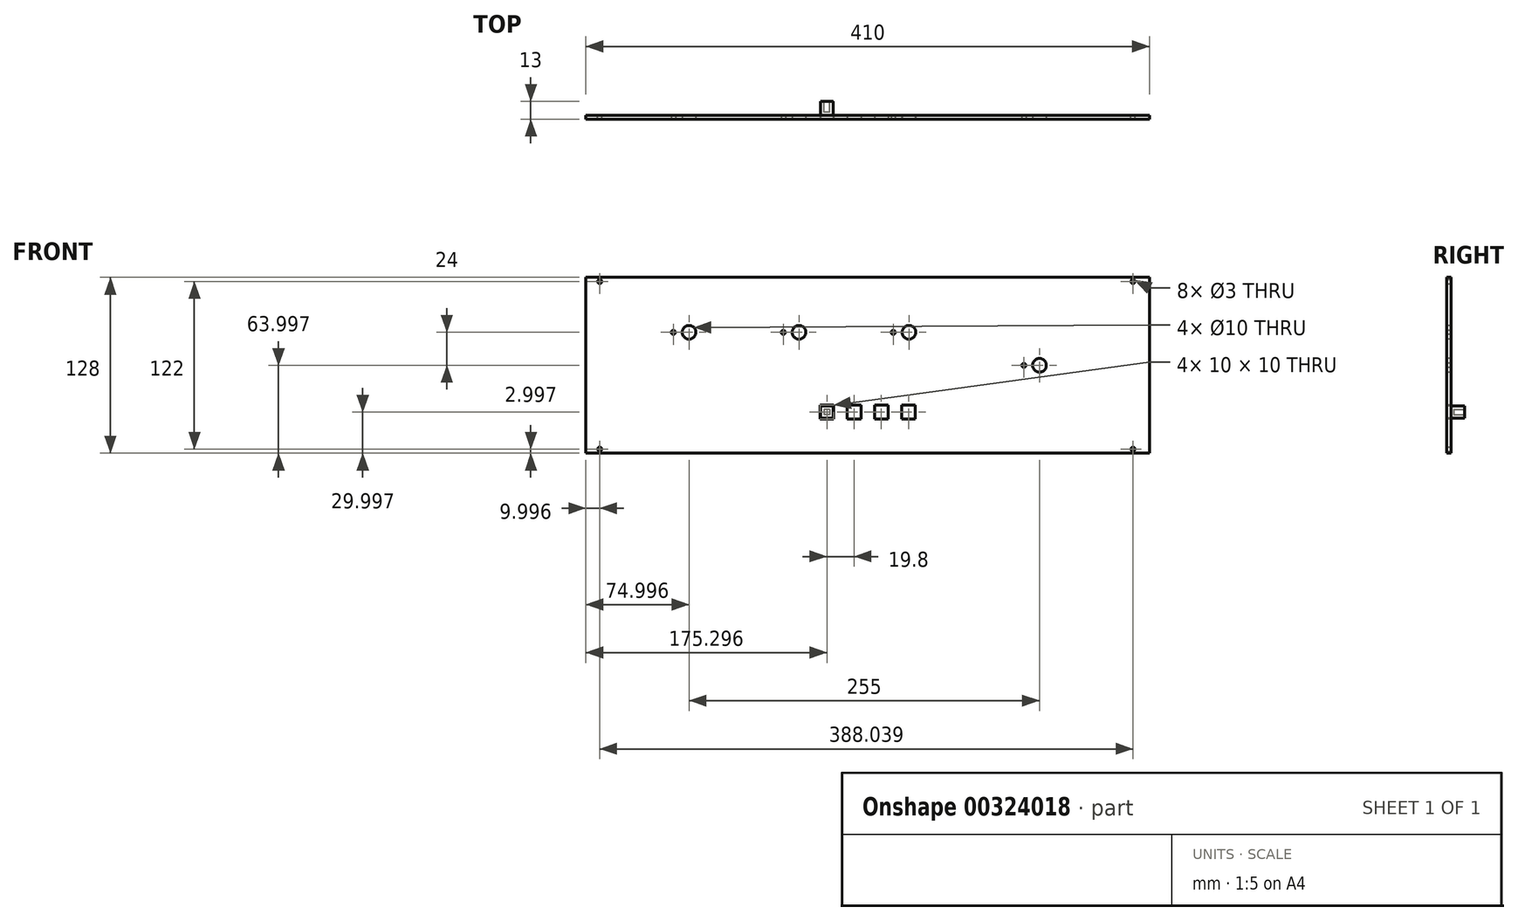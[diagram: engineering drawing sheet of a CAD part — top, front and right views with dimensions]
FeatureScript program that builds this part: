
annotation { "Feature Type Name" : "Feature", "Feature Type Description" : "" }
export const myFeature = defineFeature(function(context is Context, id is Id, definition is map)
    precondition{}
    {
        {
            var Q0;
            Q0=qCreatedBy(makeId("Front.planeOp"),FACE);
            var sketch = newSketch(context, id + "F0", { "sketchPlane" : qUnion([Q0])});
            skLineSegment(sketch, "E0.bottom", {"start": v(-121.21, 68.69) * mm, "end": v(288.79, 68.69) * mm});
            skLineSegment(sketch, "E0.top", {"start": v(-121.21, -59.31) * mm, "end": v(288.79, -59.31) * mm});
            skLineSegment(sketch, "E0.left", {"start": v(-121.21, 68.69) * mm, "end": v(-121.21, -59.31) * mm});
            skLineSegment(sketch, "E0.right", {"start": v(288.79, 68.69) * mm, "end": v(288.79, -59.31) * mm});
            skPoint(sketch, "E1", {"position": v(-111.21, 65.69) * mm});
            skPoint(sketch, "E2", {"position": v(-111.21, -56.31) * mm});
            skPoint(sketch, "E3", {"position": v(276.82, -56.31) * mm});
            skPoint(sketch, "E4", {"position": v(276.82, 65.69) * mm});
            skSolve(sketch);
        }
        {
            var Q0;
            Q0=makeQuery(id+"F0.imprint","IMPRINT",FACE,{"disambiguationData":[TD([[makeQuery(id+"F0.imprint","IMPRINT",EDGE,{"derivedFrom":sQuery(id+"F0.wireOp",EDGE,"E0.bottom")}),-1.0]])]});
            extrude(context, id + "F1", {"entities" : qUnion([Q0]), "depth" : 3 * mm});
        }
        {
            var Q0;
            Q0=sQuery(id+"F0.wireOp",VERTEX,"E1");
            var Q1;
            Q1=sQuery(id+"F0.wireOp",VERTEX,"E4");
            var Q2;
            Q2=sQuery(id+"F0.wireOp",VERTEX,"E3");
            var Q3;
            Q3=sQuery(id+"F0.wireOp",VERTEX,"E2");
            var Q4;
            Q4=makeQuery(id+"F1.opExtrude","SWEPT_BODY",BODY,{"disambiguationData":[OSD([sQuery(id+"F0.wireOp",EDGE,"E0.bottom"),sQuery(id+"F0.wireOp",EDGE,"E0.top"),sQuery(id+"F0.wireOp",EDGE,"E0.left"),sQuery(id+"F0.wireOp",EDGE,"E0.right")])]});
            hole(context, id + "F2", {"style" : HoleStyle.SIMPLE, "endStyle" : HoleEndStyle.THROUGH, "oppositeDirection" : true, "holeDiameter" : 3 * mm, "tappedDepth" : 12 * mm, "tapClearance" : 3, "locations" : qUnion([Q0, Q1, Q2, Q3]), "scope" : qUnion([Q4])});
        }
        {
            var Q0;
            Q0=makeQuery(id+"F1.opExtrude","CAP_FACE",FACE,{"disambiguationData":[OSD([sQuery(id+"F0.wireOp",EDGE,"E0.bottom"),sQuery(id+"F0.wireOp",EDGE,"E0.top"),sQuery(id+"F0.wireOp",EDGE,"E0.left"),sQuery(id+"F0.wireOp",EDGE,"E0.right")])],"isStart":false});
            var sketch = newSketch(context, id + "F3", { "sketchPlane" : qUnion([Q0])});
            skPoint(sketch, "E5", {"position": v(33.79, 28.69) * mm});
            skPoint(sketch, "E6", {"position": v(-46.21, 28.69) * mm});
            skLineSegment(sketch, "E7", {"start": v(83.79, 68.69) * mm, "end": v(83.79, -59.31) * mm});
            skCircle(sketch, "E8", {"center": v(-46.21, 28.69) * mm, "radius": 15 * mm});
            skCircle(sketch, "E9", {"center": v(33.79, 28.69) * mm, "radius": 15 * mm});
            skPoint(sketch, "E10", {"position": v(113.79, 28.69) * mm});
            skCircle(sketch, "E11", {"center": v(113.79, 28.69) * mm, "radius": 15 * mm});
            skPoint(sketch, "E12", {"position": v(208.79, 4.69) * mm});
            skCircle(sketch, "E13", {"center": v(208.79, 4.69) * mm, "radius": 20 * mm});
            skLineSegment(sketch, "E14", {"start": v(43.79, -29.31) * mm, "end": v(123.79, -29.31) * mm});
            skPoint(sketch, "E15", {"position": v(83.79, -29.31) * mm});
            skLineSegment(sketch, "E16", {"start": v(-31.21, 28.69) * mm, "end": v(18.79, 28.69) * mm, "construction": true});
            skLineSegment(sketch, "E17", {"start": v(48.79, 28.69) * mm, "end": v(98.79, 28.69) * mm, "construction": true});
            skLineSegment(sketch, "E18.bottom", {"start": v(59.09, -24.31) * mm, "end": v(49.09, -24.31) * mm});
            skLineSegment(sketch, "E18.top", {"start": v(59.09, -34.31) * mm, "end": v(49.09, -34.31) * mm});
            skLineSegment(sketch, "E18.left", {"start": v(59.09, -24.31) * mm, "end": v(59.09, -34.31) * mm});
            skLineSegment(sketch, "E18.right", {"start": v(49.09, -24.31) * mm, "end": v(49.09, -34.31) * mm});
            skPoint(sketch, "E18.middle", {"position": v(54.09, -29.31) * mm});
            skLineSegment(sketch, "E19.1.0.0", {"start": v(78.89, -24.31) * mm, "end": v(78.89, -34.31) * mm});
            skPoint(sketch, "E19.1.0.1", {"position": v(73.89, -29.31) * mm});
            skLineSegment(sketch, "E19.1.0.2", {"start": v(68.89, -24.31) * mm, "end": v(68.89, -34.31) * mm});
            skLineSegment(sketch, "E19.1.0.3", {"start": v(78.89, -24.31) * mm, "end": v(68.89, -24.31) * mm});
            skLineSegment(sketch, "E19.1.0.4", {"start": v(78.89, -34.31) * mm, "end": v(68.89, -34.31) * mm});
            skLineSegment(sketch, "E19.2.0.0", {"start": v(98.69, -24.31) * mm, "end": v(98.69, -34.31) * mm});
            skPoint(sketch, "E19.2.0.1", {"position": v(93.69, -29.31) * mm});
            skLineSegment(sketch, "E19.2.0.2", {"start": v(88.69, -24.31) * mm, "end": v(88.69, -34.31) * mm});
            skLineSegment(sketch, "E19.2.0.3", {"start": v(98.69, -24.31) * mm, "end": v(88.69, -24.31) * mm});
            skLineSegment(sketch, "E19.2.0.4", {"start": v(98.69, -34.31) * mm, "end": v(88.69, -34.31) * mm});
            skLineSegment(sketch, "E19.3.0.0", {"start": v(118.49, -24.31) * mm, "end": v(118.49, -34.31) * mm});
            skPoint(sketch, "E19.3.0.1", {"position": v(113.49, -29.31) * mm});
            skLineSegment(sketch, "E19.3.0.2", {"start": v(108.49, -24.31) * mm, "end": v(108.49, -34.31) * mm});
            skLineSegment(sketch, "E19.3.0.3", {"start": v(118.49, -24.31) * mm, "end": v(108.49, -24.31) * mm});
            skLineSegment(sketch, "E19.3.0.4", {"start": v(118.49, -34.31) * mm, "end": v(108.49, -34.31) * mm});
            skLineSegment(sketch, "E19.direction1", {"start": v(49.09, -34.31) * mm, "end": v(68.89, -34.31) * mm, "construction": true});
            skLineSegment(sketch, "E20", {"start": v(73.89, -29.31) * mm, "end": v(93.69, -29.31) * mm});
            skLineSegment(sketch, "E21", {"start": v(49.09, -34.31) * mm, "end": v(49.09, -59.31) * mm, "construction": true});
            skLineSegment(sketch, "E22", {"start": v(-46.21, 43.69) * mm, "end": v(-46.21, 68.69) * mm, "construction": true});
            skLineSegment(sketch, "E23", {"start": v(-61.21, 28.69) * mm, "end": v(-121.21, 28.69) * mm, "construction": true});
            skLineSegment(sketch, "E24", {"start": v(228.79, 4.69) * mm, "end": v(288.79, 4.69) * mm, "construction": true});
            skCircle(sketch, "E25", {"center": v(-46.21, 28.69) * mm, "radius": 11.38 * mm, "construction": true});
            skCircle(sketch, "E26", {"center": v(-57.59, 28.69) * mm, "radius": 1.5 * mm});
            skCircle(sketch, "E27.1.0.0", {"center": v(33.79, 28.69) * mm, "radius": 11.38 * mm, "construction": true});
            skCircle(sketch, "E27.1.0.1", {"center": v(22.41, 28.69) * mm, "radius": 1.5 * mm});
            skCircle(sketch, "E27.2.0.0", {"center": v(113.79, 28.69) * mm, "radius": 11.38 * mm, "construction": true});
            skCircle(sketch, "E27.2.0.1", {"center": v(102.41, 28.69) * mm, "radius": 1.5 * mm});
            skLineSegment(sketch, "E27.direction1", {"start": v(-57.59, 28.69) * mm, "end": v(22.41, 28.69) * mm, "construction": true});
            skCircle(sketch, "E28.2.0.0", {"center": v(208.79, 4.69) * mm, "radius": 11.38 * mm, "construction": true});
            skCircle(sketch, "E28.2.0.1", {"center": v(197.41, 4.69) * mm, "radius": 1.5 * mm});
            skLineSegment(sketch, "E29", {"start": v(83.79, 4.69) * mm, "end": v(208.79, 4.69) * mm, "construction": true});
            skSolve(sketch);
        }
        {
            var Q0;
            Q0=sQuery(id+"F3.wireOp",VERTEX,"E6");
            var Q1;
            Q1=sQuery(id+"F3.wireOp",VERTEX,"E5");
            var Q2;
            Q2=sQuery(id+"F3.wireOp",VERTEX,"E10");
            var Q3;
            Q3=sQuery(id+"F3.wireOp",VERTEX,"E12");
            var Q4;
            Q4=makeQuery(id+"F1.opExtrude","SWEPT_BODY",BODY,{"disambiguationData":[OSD([sQuery(id+"F0.wireOp",EDGE,"E0.bottom"),sQuery(id+"F0.wireOp",EDGE,"E0.top"),sQuery(id+"F0.wireOp",EDGE,"E0.left"),sQuery(id+"F0.wireOp",EDGE,"E0.right")])]});
            hole(context, id + "F4", {"style" : HoleStyle.SIMPLE, "endStyle" : HoleEndStyle.THROUGH, "holeDiameter" : 10 * mm, "tappedDepth" : 12 * mm, "tapClearance" : 3, "locations" : qUnion([Q0, Q1, Q2, Q3]), "scope" : qUnion([Q4])});
        }
        {
            var Q0;
            {var subQ5=sQuery(id+"F3.wireOp",EDGE,"E18.top");Q0=makeQuery(id+"F3.imprint","IMPRINT",FACE,{"disambiguationData":[TD([[makeQuery(id+"F3.imprint","IMPRINT",EDGE,{"derivedFrom":subQ5}),-1.0]])]});}
            var Q1;
            {var subQ5=sQuery(id+"F3.wireOp",EDGE,"E18.bottom");Q1=makeQuery(id+"F3.imprint","IMPRINT",FACE,{"disambiguationData":[TD([[makeQuery(id+"F3.imprint","IMPRINT",EDGE,{"derivedFrom":subQ5}),1.0]])]});}
            var Q2;
            {var subQ0=sQuery(id+"F3.wireOp",EDGE,"E19.1.0.3");Q2=makeQuery(id+"F3.imprint","IMPRINT",FACE,{"disambiguationData":[TD([[makeQuery(id+"F3.imprint","IMPRINT",EDGE,{"derivedFrom":subQ0}),1.0]])]});}
            var Q3;
            {var subQ0=sQuery(id+"F3.wireOp",EDGE,"E19.1.0.4");Q3=makeQuery(id+"F3.imprint","IMPRINT",FACE,{"disambiguationData":[TD([[makeQuery(id+"F3.imprint","IMPRINT",EDGE,{"derivedFrom":subQ0}),-1.0]])]});}
            var Q4;
            {var subQ0=sQuery(id+"F3.wireOp",EDGE,"E19.2.0.4");Q4=makeQuery(id+"F3.imprint","IMPRINT",FACE,{"disambiguationData":[TD([[makeQuery(id+"F3.imprint","IMPRINT",EDGE,{"derivedFrom":subQ0}),-1.0]])]});}
            var Q5;
            {var subQ0=sQuery(id+"F3.wireOp",EDGE,"E19.2.0.3");Q5=makeQuery(id+"F3.imprint","IMPRINT",FACE,{"disambiguationData":[TD([[makeQuery(id+"F3.imprint","IMPRINT",EDGE,{"derivedFrom":subQ0}),1.0]])]});}
            var Q6;
            {var subQ5=sQuery(id+"F3.wireOp",EDGE,"E19.3.0.3");Q6=makeQuery(id+"F3.imprint","IMPRINT",FACE,{"disambiguationData":[TD([[makeQuery(id+"F3.imprint","IMPRINT",EDGE,{"derivedFrom":subQ5}),1.0]])]});}
            var Q7;
            {var subQ5=sQuery(id+"F3.wireOp",EDGE,"E19.3.0.4");Q7=makeQuery(id+"F3.imprint","IMPRINT",FACE,{"disambiguationData":[TD([[makeQuery(id+"F3.imprint","IMPRINT",EDGE,{"derivedFrom":subQ5}),-1.0]])]});}
            extrude(context, id + "F5", {"entities" : qUnion([Q0, Q1, Q2, Q3, Q4, Q5, Q6, Q7]), "operationType" : NewBodyOperationType.REMOVE, "endBound" : BoundingType.UP_TO_NEXT, "oppositeDirection" : true, "depth" : 25 * mm});
        }
        {
            var Q0;
            Q0=makeQuery(id+"F3.imprint","IMPRINT",FACE,{"disambiguationData":[TD([[makeQuery(id+"F3.imprint","IMPRINT",EDGE,{"derivedFrom":sQuery(id+"F3.wireOp",EDGE,"E26")}),1.0]])]});
            var Q1;
            Q1=makeQuery(id+"F3.imprint","IMPRINT",FACE,{"disambiguationData":[TD([[makeQuery(id+"F3.imprint","IMPRINT",EDGE,{"derivedFrom":sQuery(id+"F3.wireOp",EDGE,"E27.1.0.1")}),1.0]])]});
            var Q2;
            Q2=makeQuery(id+"F3.imprint","IMPRINT",FACE,{"disambiguationData":[TD([[makeQuery(id+"F3.imprint","IMPRINT",EDGE,{"derivedFrom":sQuery(id+"F3.wireOp",EDGE,"E27.2.0.1")}),1.0]])]});
            var Q3;
            Q3=makeQuery(id+"F3.imprint","IMPRINT",FACE,{"disambiguationData":[TD([[makeQuery(id+"F3.imprint","IMPRINT",EDGE,{"derivedFrom":sQuery(id+"F3.wireOp",EDGE,"E28.2.0.1")}),1.0]])]});
            extrude(context, id + "F6", {"entities" : qUnion([Q0, Q1, Q2, Q3]), "operationType" : NewBodyOperationType.REMOVE, "endBound" : BoundingType.UP_TO_NEXT, "oppositeDirection" : true, "depth" : 25 * mm});
        }
        {
            var Q0;
            Q0=makeQuery(id+"F3.imprint","IMPRINT",FACE,{"disambiguationData":[TD([[makeQuery(id+"F3.imprint","IMPRINT",EDGE,{"derivedFrom":sQuery(id+"F3.wireOp",EDGE,"E8")}),-1.0]])]});
            var sketch = newSketch(context, id + "F7", { "sketchPlane" : qUnion([Q0])});
            skLineSegment(sketch, "E30.bottom", {"start": v(49.59, -24.81) * mm, "end": v(58.59, -24.81) * mm});
            skLineSegment(sketch, "E30.top", {"start": v(49.59, -33.81) * mm, "end": v(58.59, -33.81) * mm});
            skLineSegment(sketch, "E30.left", {"start": v(49.59, -24.81) * mm, "end": v(49.59, -33.81) * mm});
            skLineSegment(sketch, "E30.right", {"start": v(58.59, -24.81) * mm, "end": v(58.59, -33.81) * mm});
            skLineSegment(sketch, "E31", {"start": v(58.59, -24.81) * mm, "end": v(59.09, -24.81) * mm, "construction": true});
            skLineSegment(sketch, "E32", {"start": v(49.59, -24.81) * mm, "end": v(49.59, -24.31) * mm, "construction": true});
            skLineSegment(sketch, "E33", {"start": v(49.59, -33.81) * mm, "end": v(49.09, -33.81) * mm, "construction": true});
            skLineSegment(sketch, "E34", {"start": v(58.59, -33.81) * mm, "end": v(58.59, -34.31) * mm, "construction": true});
            skSolve(sketch);
        }
        {
            var Q0;
            Q0=makeQuery(id+"F7.imprint","IMPRINT",FACE,{"disambiguationData":[TD([[makeQuery(id+"F7.imprint","IMPRINT",EDGE,{"derivedFrom":sQuery(id+"F7.wireOp",EDGE,"E30.bottom")}),-1.0]])]});
            extrude(context, id + "F8", {"entities" : qUnion([Q0]), "oppositeDirection" : true, "depth" : (8 + 5) * mm});
        }
        {
            var Q0;
            Q0=makeQuery(id+"F8.opExtrude","SWEPT_EDGE",EDGE,{"disambiguationData":[OSD([sQuery(id+"F7.wireOp",EDGE,"E30.bottom"),sQuery(id+"F7.wireOp",EDGE,"E30.right")])]});
            var Q1;
            Q1=makeQuery(id+"F8.opExtrude","SWEPT_EDGE",EDGE,{"disambiguationData":[OSD([sQuery(id+"F7.wireOp",EDGE,"E30.bottom"),sQuery(id+"F7.wireOp",EDGE,"E30.left")])]});
            var Q2;
            Q2=makeQuery(id+"F8.opExtrude","SWEPT_EDGE",EDGE,{"disambiguationData":[OSD([sQuery(id+"F7.wireOp",EDGE,"E30.top"),sQuery(id+"F7.wireOp",EDGE,"E30.right")])]});
            var Q3;
            Q3=makeQuery(id+"F8.opExtrude","SWEPT_EDGE",EDGE,{"disambiguationData":[OSD([sQuery(id+"F7.wireOp",EDGE,"E30.top"),sQuery(id+"F7.wireOp",EDGE,"E30.left")])]});
            fillet(context, id + "F9", {"entities" : qUnion([Q0, Q1, Q2, Q3]), "radius" : 1.5 * mm, "tangentPropagation" : true, "allowEdgeOverflow" : false});
        }
        {
            var Q0;
            Q0=makeQuery(id+"F8.opExtrude","CAP_FACE",FACE,{"disambiguationData":[OSD([sQuery(id+"F7.wireOp",EDGE,"E30.bottom"),sQuery(id+"F7.wireOp",EDGE,"E30.top"),sQuery(id+"F7.wireOp",EDGE,"E30.left"),sQuery(id+"F7.wireOp",EDGE,"E30.right")])],"isStart":false});
            var sketch = newSketch(context, id + "F10", { "sketchPlane" : qUnion([Q0])});
            skLineSegment(sketch, "E35.bottom", {"start": v(-56.09, -27.31) * mm, "end": v(-52.09, -27.31) * mm});
            skLineSegment(sketch, "E35.top", {"start": v(-56.09, -31.31) * mm, "end": v(-52.09, -31.31) * mm});
            skLineSegment(sketch, "E35.left", {"start": v(-56.09, -27.31) * mm, "end": v(-56.09, -31.31) * mm});
            skLineSegment(sketch, "E35.right", {"start": v(-52.09, -27.31) * mm, "end": v(-52.09, -31.31) * mm});
            skLineSegment(sketch, "E36", {"start": v(-54.09, -27.31) * mm, "end": v(-54.09, -24.81) * mm, "construction": true});
            skLineSegment(sketch, "E37", {"start": v(-52.09, -29.31) * mm, "end": v(-49.59, -29.31) * mm, "construction": true});
            skLineSegment(sketch, "E38", {"start": v(-56.09, -29.31) * mm, "end": v(-58.59, -29.31) * mm, "construction": true});
            skLineSegment(sketch, "E39", {"start": v(-54.09, -31.31) * mm, "end": v(-54.09, -33.81) * mm, "construction": true});
            skSolve(sketch);
        }
        {
            var Q0;
            Q0=makeQuery(id+"F10.imprint","IMPRINT",FACE,{"disambiguationData":[TD([[makeQuery(id+"F10.imprint","IMPRINT",EDGE,{"derivedFrom":sQuery(id+"F10.wireOp",EDGE,"E35.bottom")}),-1.0]])]});
            extrude(context, id + "F11", {"entities" : qUnion([Q0]), "operationType" : NewBodyOperationType.REMOVE, "oppositeDirection" : true, "depth" : 8 * mm});
        }
    });
